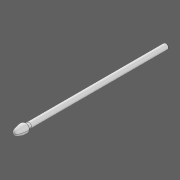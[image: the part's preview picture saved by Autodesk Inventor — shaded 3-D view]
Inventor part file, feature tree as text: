
AUTODESK INVENTOR PART (.ipt)
format: ipt  version: 2020 (Build 240168000, 168)  size: 114,176 bytes
history: native  units: in
note: dims shown in document units (in); Inventor stores cm internally (conversion verified against a paired STEP export)
features: revolve x1, fillet x1, sketch x1
ambient origin geometry x8: Origin, YZ Plane, XZ Plane, XY Plane, X Axis, Y Axis, Z Axis, Center Point
bodies: Solid1 (feature_tree)
feature tree (3):
  revolve  "Revolution1"  [1 undecoded]
  fillet  "Fillet1"  Radius=7.0866in
  sketch  "Sketch1"  dims[d0=90.0deg d2=0.5906in d5=7.0866in d6=0.1575in d8=0.1969in d9=0.2362in d10=0.1969in d11=0.1969in d12=0.2362in d13=0.2756in]
note: 1 required parameter value undecoded (feature->parameter linkage not recoverable at this tier; creation-order binding heuristic only, values carry confidence <= 0.55)
